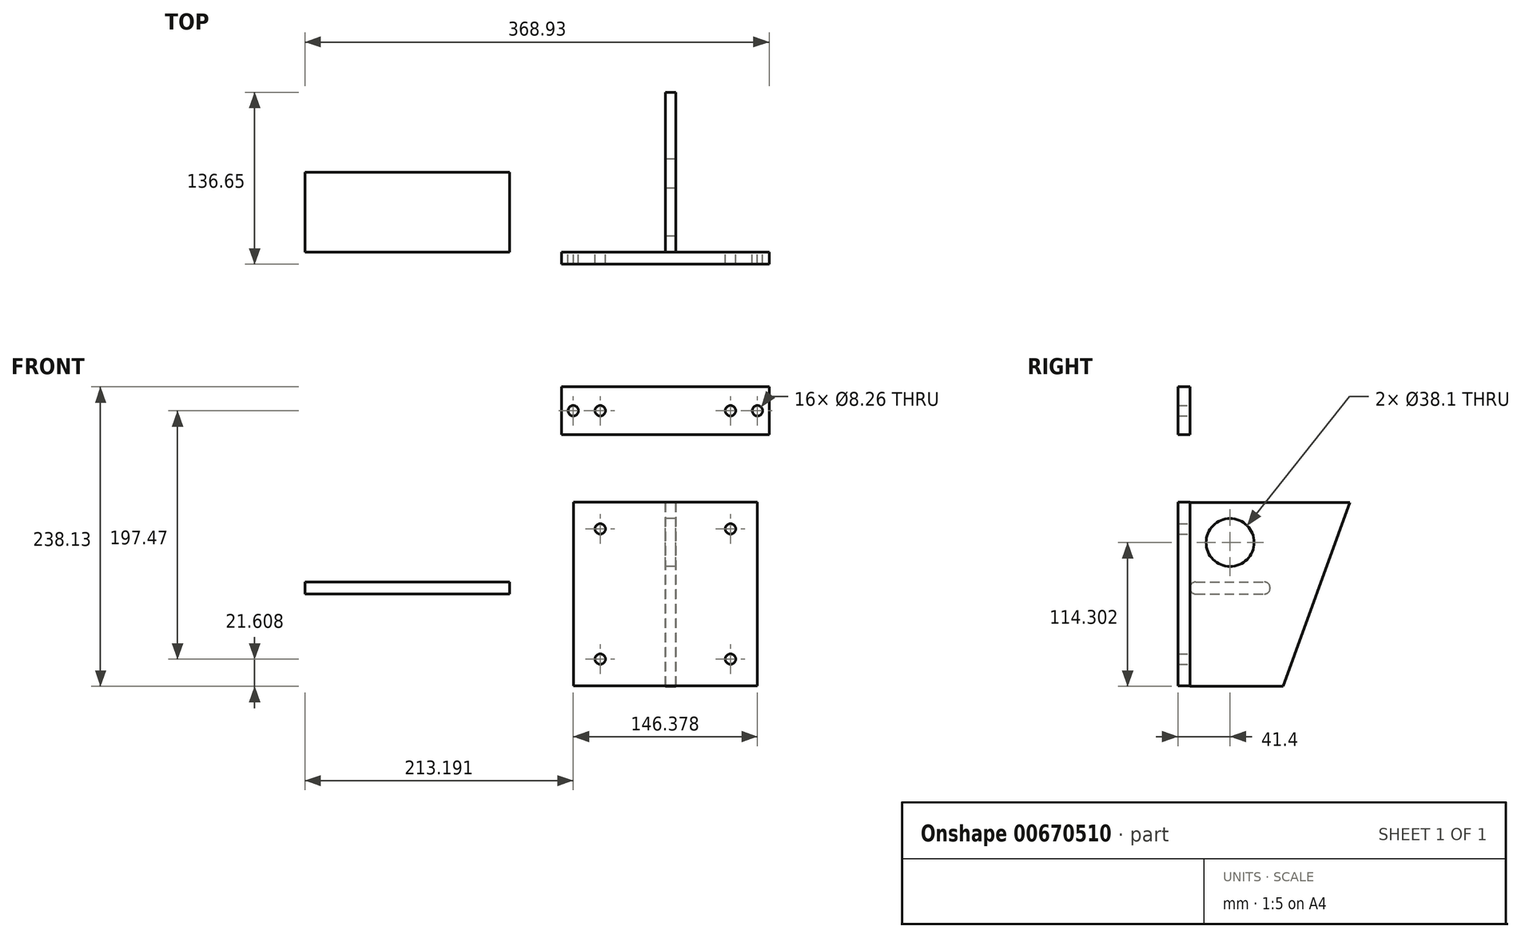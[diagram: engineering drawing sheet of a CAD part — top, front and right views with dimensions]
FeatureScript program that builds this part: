
annotation { "Feature Type Name" : "Feature", "Feature Type Description" : "" }
export const myFeature = defineFeature(function(context is Context, id is Id, definition is map)
    precondition{}
    {
        {
            var Q0;
            Q0=qCreatedBy(makeId("Front.planeOp"),FACE);
            var sketch = newSketch(context, id + "F0", { "sketchPlane" : qUnion([Q0])});
            skLineSegment(sketch, "E0.bottom", {"start": v(73.03, -73.02) * mm, "end": v(-73.03, -73.03) * mm});
            skLineSegment(sketch, "E0.top", {"start": v(73.03, 73.03) * mm, "end": v(-73.03, 73.02) * mm});
            skLineSegment(sketch, "E0.left", {"start": v(73.03, -73.03) * mm, "end": v(73.03, 73.03) * mm});
            skLineSegment(sketch, "E0.right", {"start": v(-73.03, -73.03) * mm, "end": v(-73.03, 73.02) * mm});
            skPoint(sketch, "E0.middle", {"position": v(0, 0) * mm});
            skLineSegment(sketch, "E1.bottom", {"start": v(47.63, -47.62) * mm, "end": v(-47.63, -47.63) * mm});
            skLineSegment(sketch, "E1.top", {"start": v(47.63, 47.63) * mm, "end": v(-47.63, 47.62) * mm});
            skLineSegment(sketch, "E1.left", {"start": v(47.63, -47.62) * mm, "end": v(47.63, 47.63) * mm});
            skLineSegment(sketch, "E1.right", {"start": v(-47.63, -47.63) * mm, "end": v(-47.63, 47.62) * mm});
            skCircle(sketch, "E2", {"center": v(-51.75, 51.75) * mm, "radius": 4.13 * mm});
            skCircle(sketch, "E3", {"center": v(-51.75, -51.75) * mm, "radius": 4.13 * mm});
            skCircle(sketch, "E4.MirrorC", {"center": v(51.75, -51.75) * mm, "radius": 4.13 * mm});
            skCircle(sketch, "E5.MirrorC", {"center": v(51.75, 51.75) * mm, "radius": 4.13 * mm});
            skSolve(sketch);
        }
        {
            var Q0;
            Q0=makeQuery(id+"F0.imprint","IMPRINT",FACE,{"disambiguationData":[TD([[makeQuery(id+"F0.imprint","IMPRINT",EDGE,{"derivedFrom":sQuery(id+"F0.wireOp",EDGE,"E0.bottom")}),-1.0]])]});
            var Q1;
            Q1=makeQuery(id+"F0.imprint","IMPRINT",FACE,{"disambiguationData":[TD([[makeQuery(id+"F0.imprint","IMPRINT",EDGE,{"derivedFrom":sQuery(id+"F0.wireOp",EDGE,"E1.bottom")}),-1.0]])]});
            var Q2;
            Q2=sQuery(id+"F0.wireOp",EDGE,"E0.top");
            var Q3;
            Q3=sQuery(id+"F0.wireOp",EDGE,"E0.right");
            var Q4;
            Q4=sQuery(id+"F0.wireOp",EDGE,"E0.bottom");
            var Q5;
            Q5=sQuery(id+"F0.wireOp",EDGE,"E0.left");
            var Q6;
            Q6=sQuery(id+"F0.wireOp",EDGE,"E5.MirrorC");
            var Q7;
            Q7=sQuery(id+"F0.wireOp",EDGE,"E4.MirrorC");
            var Q8;
            Q8=sQuery(id+"F0.wireOp",EDGE,"E3");
            var Q9;
            Q9=sQuery(id+"F0.wireOp",EDGE,"E2");
            extrude(context, id + "F1", {"entities" : qUnion([Q0, Q1]), "surfaceEntities" : qUnion([Q2, Q3, Q4, Q5, Q6, Q7, Q8, Q9]), "depth" : 9.52 * mm, "offsetDistance" : 25.4 * mm});
        }
        {
            var Q0;
            Q0=qCreatedBy(makeId("Right.planeOp"),FACE);
            var sketch = newSketch(context, id + "F2", { "sketchPlane" : qUnion([Q0])});
            skLineSegment(sketch, "E6", {"start": v(0, -73.36) * mm, "end": v(0, 72.7) * mm});
            skLineSegment(sketch, "E7", {"start": v(0, 72.7) * mm, "end": v(127, 72.7) * mm});
            skLineSegment(sketch, "E8", {"start": v(127, 72.7) * mm, "end": v(73.84, -73.36) * mm});
            skLineSegment(sketch, "E9", {"start": v(73.84, -73.36) * mm, "end": v(0, -73.36) * mm});
            skCircle(sketch, "E10", {"center": v(31.75, 40.94) * mm, "radius": 19.05 * mm});
            skSolve(sketch);
        }
        {
            var Q0;
            Q0=makeQuery(id+"F2.imprint","IMPRINT",FACE,{"disambiguationData":[TD([[makeQuery(id+"F2.imprint","IMPRINT",EDGE,{"derivedFrom":sQuery(id+"F2.wireOp",EDGE,"E6")}),-1.0]])]});
            extrude(context, id + "F3", {"entities" : qUnion([Q0]), "depth" : 8.25 * mm, "offsetDistance" : 25.4 * mm});
        }
        {
            var Q0;
            Q0=qCreatedBy(makeId("Top.planeOp"),FACE);
            var sketch = newSketch(context, id + "F4", { "sketchPlane" : qUnion([Q0])});
            skLineSegment(sketch, "E11.bottom", {"start": v(-123.83, 0) * mm, "end": v(-286.39, 0) * mm});
            skLineSegment(sketch, "E11.top", {"start": v(-123.83, 63.5) * mm, "end": v(-286.39, 63.5) * mm});
            skLineSegment(sketch, "E11.left", {"start": v(-123.83, 0) * mm, "end": v(-123.83, 63.5) * mm});
            skLineSegment(sketch, "E11.right", {"start": v(-286.39, 0) * mm, "end": v(-286.39, 63.5) * mm});
            skSolve(sketch);
        }
        {
            var Q0;
            Q0=makeQuery(id+"F4.imprint","IMPRINT",FACE,{"disambiguationData":[TD([[makeQuery(id+"F4.imprint","IMPRINT",EDGE,{"derivedFrom":sQuery(id+"F4.wireOp",EDGE,"E11.bottom")}),-1.0]])]});
            extrude(context, id + "F5", {"entities" : qUnion([Q0]), "depth" : 9.52 * mm, "offsetDistance" : 25.4 * mm});
        }
        {
            var Q0;
            Q0=makeQuery(id+"F5.opExtrude","CAP_EDGE",EDGE,{"disambiguationData":[OSD([sQuery(id+"F4.wireOp",EDGE,"E11.bottom")])],"isStart":false});
            var Q1;
            Q1=makeQuery(id+"F5.opExtrude","CAP_EDGE",EDGE,{"disambiguationData":[OSD([sQuery(id+"F4.wireOp",EDGE,"E11.bottom")])],"isStart":true});
            var Q2;
            Q2=makeQuery(id+"F5.opExtrude","CAP_EDGE",EDGE,{"disambiguationData":[OSD([sQuery(id+"F4.wireOp",EDGE,"E11.top")])],"isStart":false});
            var Q3;
            Q3=makeQuery(id+"F5.opExtrude","CAP_EDGE",EDGE,{"disambiguationData":[OSD([sQuery(id+"F4.wireOp",EDGE,"E11.top")])],"isStart":true});
            fillet(context, id + "F6", {"entities" : qUnion([Q0, Q1, Q2, Q3]), "radius" : 4.44 * mm, "tangentPropagation" : true, "allowEdgeOverflow" : false});
        }
        {
            var Q0;
            Q0=qCreatedBy(makeId("Front.planeOp"),FACE);
            var sketch = newSketch(context, id + "F7", { "sketchPlane" : qUnion([Q0])});
            skLineSegment(sketch, "E12.bottom", {"start": v(-82.55, 164.77) * mm, "end": v(82.55, 164.77) * mm});
            skLineSegment(sketch, "E12.top", {"start": v(-82.55, 126.67) * mm, "end": v(82.55, 126.67) * mm});
            skLineSegment(sketch, "E12.left", {"start": v(-82.55, 164.77) * mm, "end": v(-82.55, 126.67) * mm});
            skLineSegment(sketch, "E12.right", {"start": v(82.55, 164.77) * mm, "end": v(82.55, 126.67) * mm});
            skCircle(sketch, "E13", {"center": v(-73.19, 145.72) * mm, "radius": 4.13 * mm});
            skCircle(sketch, "E14", {"center": v(-51.75, 145.7) * mm, "radius": 4.13 * mm});
            skCircle(sketch, "E15.MirrorC", {"center": v(51.75, 145.7) * mm, "radius": 4.13 * mm});
            skCircle(sketch, "E16.MirrorC", {"center": v(73.19, 145.72) * mm, "radius": 4.13 * mm});
            skSolve(sketch);
        }
        {
            var Q0;
            Q0=makeQuery(id+"F7.imprint","IMPRINT",FACE,{"disambiguationData":[TD([[makeQuery(id+"F7.imprint","IMPRINT",EDGE,{"derivedFrom":sQuery(id+"F7.wireOp",EDGE,"E12.bottom")}),-1.0]])]});
            extrude(context, id + "F8", {"entities" : qUnion([Q0]), "depth" : 9.65 * mm, "offsetDistance" : 25.4 * mm});
        }
    });
